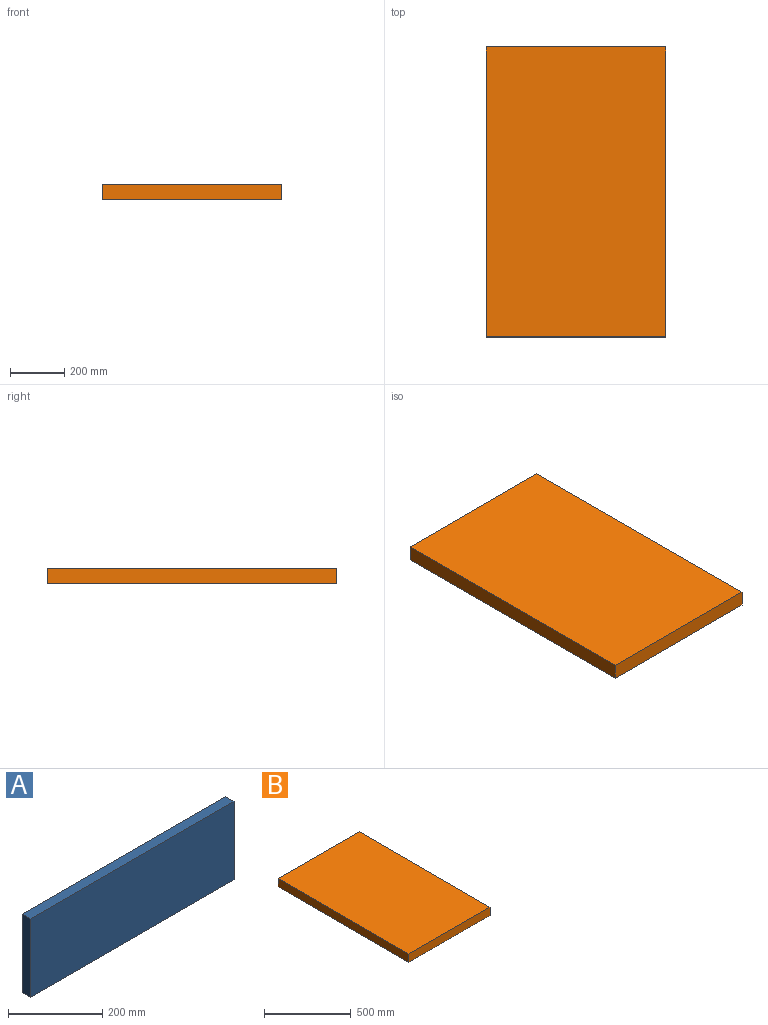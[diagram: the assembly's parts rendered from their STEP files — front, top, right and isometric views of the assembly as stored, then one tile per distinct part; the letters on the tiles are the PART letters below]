
ASSEMBLY  parts=2 mates=1
PART A: 6 faces, bbox 609.6x25.4x203.2 mm
  f0: plane 609.6x203.2mm, normal (0,1,0), area 123870.7mm2, adj f1,f3,f4,f5
  f1: plane 609.6x25.4mm, normal (0,0,1), area 15483.8mm2, adj f0,f2,f4,f5
  f2: plane 609.6x203.2mm, normal (0,-1,0), area 123870.7mm2, adj f1,f3,f4,f5
  f3: plane 609.6x25.4mm, normal (0,0,-1), area 15483.8mm2, adj f0,f2,f4,f5
  f4: plane 203.2x25.4mm, normal (1,0,0), area 5161.3mm2, adj f0,f1,f2,f3
  f5: plane 203.2x25.4mm, normal (-1,0,0), area 5161.3mm2, adj f0,f1,f2,f3
PART B: 11 faces, bbox 660.4x1066.8x58.4 mm
  f0: plane 1066.8x660.4mm, normal (0,0,-1), area 64354.7mm2, adj f1,f3,f4,f5,f6,f8,f9,f10
  f1: plane 1066.8x58.42mm, normal (1,0,0), area 62322.5mm2, adj f0,f2,f4,f5
  f2: plane 1066.8x660.4mm, normal (0,0,1), area 704514.7mm2, adj f1,f3,f4,f5
  f3: plane 1066.8x58.42mm, normal (-1,0,0), area 62322.5mm2, adj f0,f2,f4,f5
  f4: plane 660.4x58.42mm, normal (0,1,0), area 38580.6mm2, adj f0,f1,f2,f3
  f5: plane 660.4x58.42mm, normal (0,-1,0), area 38580.6mm2, adj f0,f1,f2,f3
  f6: plane 1028.7x39.37mm, normal (-1,0,0), area 40499.9mm2, adj f0,f7,f9,f10
  f7: plane 1028.7x622.3mm, normal (0,0,-1), area 640160mm2, adj f6,f8,f9,f10
  f8: plane 1028.7x39.37mm, normal (1,0,0), area 40499.9mm2, adj f0,f7,f9,f10
  f9: plane 622.3x39.37mm, normal (0,-1,0), area 24500mm2, adj f0,f6,f7,f8
  f10: plane 622.3x39.37mm, normal (0,1,0), area 24500mm2, adj f0,f6,f7,f8
PLACE A rot(axis=(-1,0,0),90deg) t=(0,120.65,-9.52)mm
PLACE B at identity
MATE fastened A.f3 <-> B.f10  axis (0,-1,0) through (0,19.05,-9.52)mm
